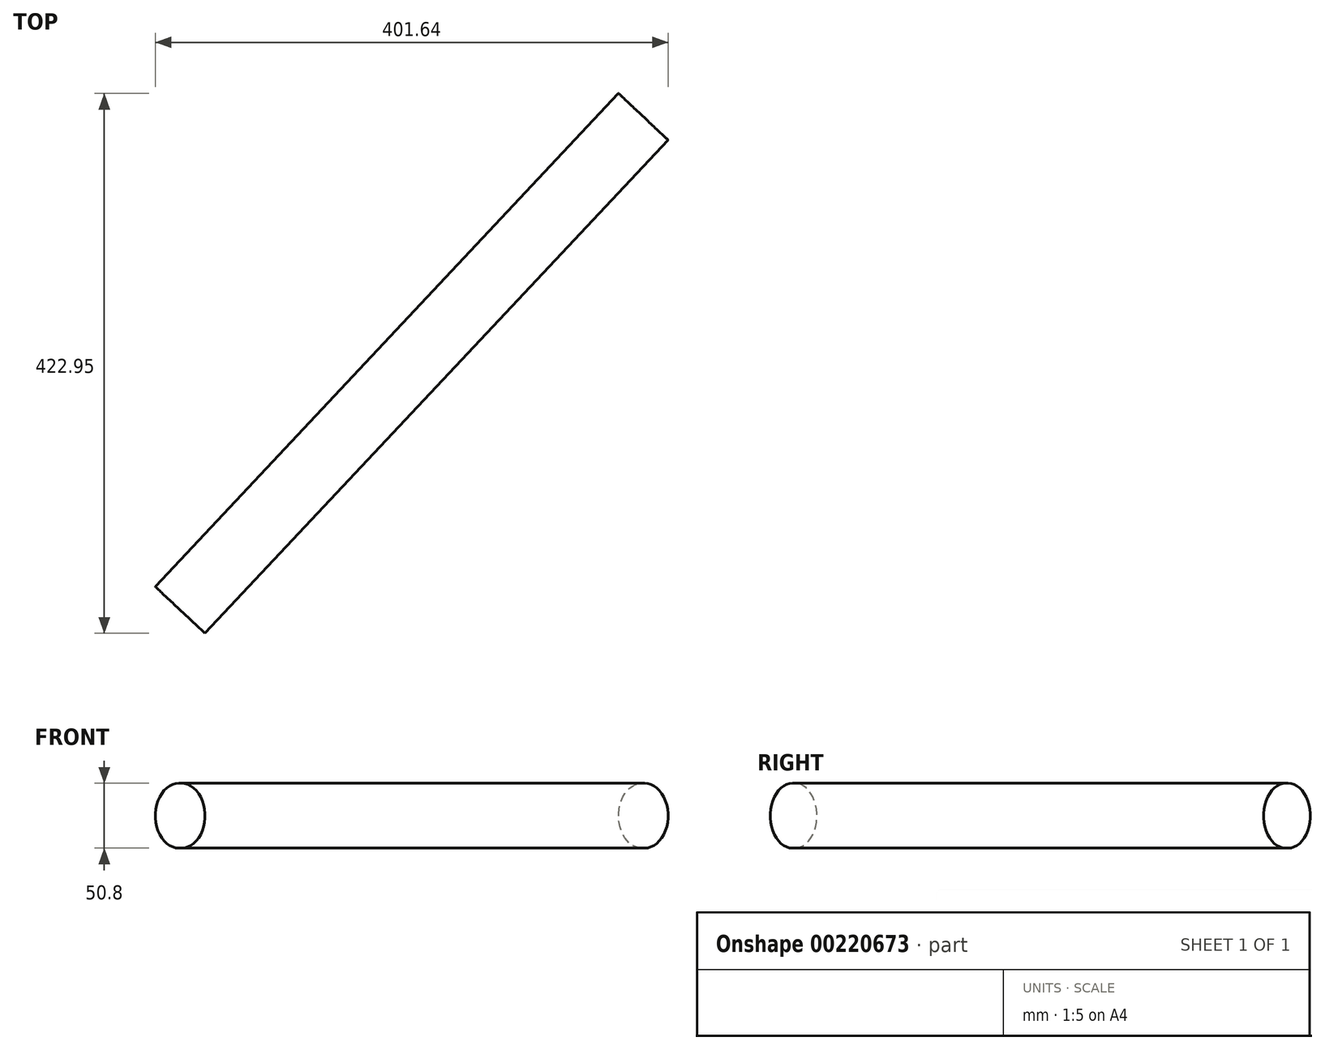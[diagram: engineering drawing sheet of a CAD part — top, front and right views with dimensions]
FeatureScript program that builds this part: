
annotation { "Feature Type Name" : "Feature", "Feature Type Description" : "" }
export const myFeature = defineFeature(function(context is Context, id is Id, definition is map)
    precondition{}
    {
        {
            var Q0;
            Q0=qCreatedBy(makeId("Top.planeOp"),FACE);
            var sketch = newSketch(context, id + "F0", { "sketchPlane" : qUnion([Q0])});
            skLineSegment(sketch, "E0", {"start": v(0, 0) * mm, "end": v(362.75, 386.44) * mm});
            skLineSegment(sketch, "E1.0", {"start": v(-38.9, 36.5) * mm, "end": v(323.85, 422.95) * mm});
            skLineSegment(sketch, "E2", {"start": v(-38.9, 36.5) * mm, "end": v(0, 0) * mm});
            skLineSegment(sketch, "E3", {"start": v(323.85, 422.95) * mm, "end": v(362.75, 386.44) * mm});
            skSolve(sketch);
        }
        {
            var Q0;
            Q0=makeQuery(id+"F0.imprint","IMPRINT",FACE,{"disambiguationData":[TD([[makeQuery(id+"F0.imprint","IMPRINT",EDGE,{"derivedFrom":sQuery(id+"F0.wireOp",EDGE,"E0")}),1.0]])]});
            extrude(context, id + "F1", {"entities" : qUnion([Q0]), "depth" : 50.8 * mm});
        }
        {
            var Q0;
            Q0=makeQuery(id+"F1.opExtrude","CAP_EDGE",EDGE,{"disambiguationData":[OSD([sQuery(id+"F0.wireOp",EDGE,"E1.0")])],"isStart":false});
            var Q1;
            Q1=makeQuery(id+"F1.opExtrude","CAP_EDGE",EDGE,{"disambiguationData":[OSD([sQuery(id+"F0.wireOp",EDGE,"E0")])],"isStart":false});
            var Q2;
            Q2=makeQuery(id+"F1.opExtrude","CAP_EDGE",EDGE,{"disambiguationData":[OSD([sQuery(id+"F0.wireOp",EDGE,"E0")])],"isStart":true});
            var Q3;
            Q3=makeQuery(id+"F1.opExtrude","CAP_EDGE",EDGE,{"disambiguationData":[OSD([sQuery(id+"F0.wireOp",EDGE,"E1.0")])],"isStart":true});
            fillet(context, id + "F2", {"entities" : qUnion([Q0, Q1, Q2, Q3]), "radius" : 25.4 * mm, "tangentPropagation" : true, "allowEdgeOverflow" : false});
        }
    });
